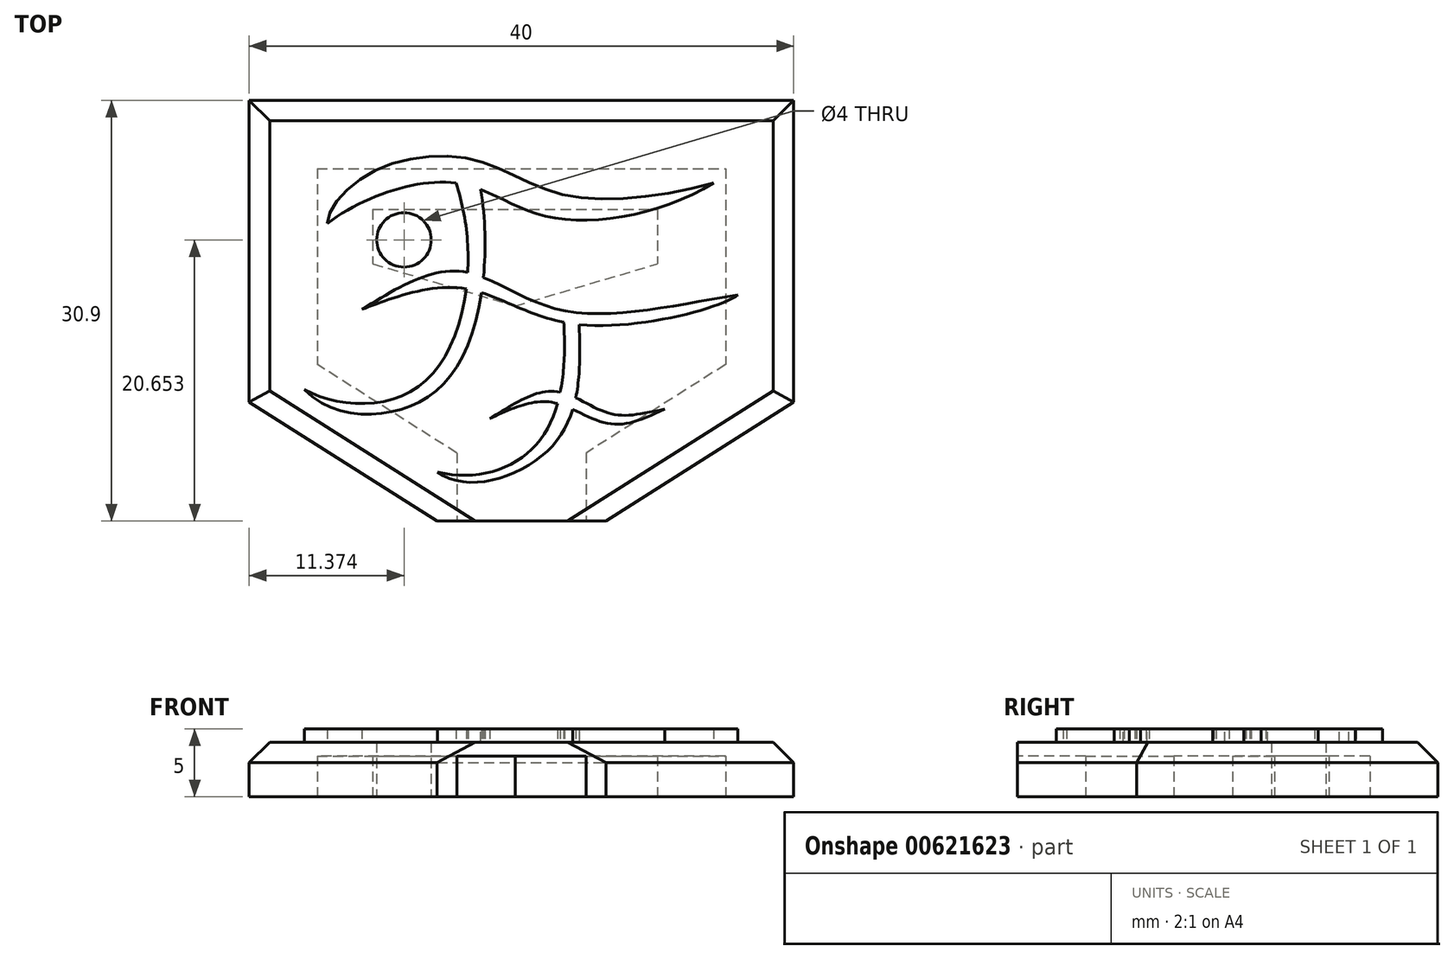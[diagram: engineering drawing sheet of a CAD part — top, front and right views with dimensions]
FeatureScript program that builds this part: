
annotation { "Feature Type Name" : "Feature", "Feature Type Description" : "" }
export const myFeature = defineFeature(function(context is Context, id is Id, definition is map)
    precondition{}
    {
        {
            var Q0;
            Q0=qCreatedBy(makeId("Top.planeOp"),FACE);
            var sketch = newSketch(context, id + "F0", { "sketchPlane" : qUnion([Q0])});
            skLineSegment(sketch, "E0.bottom", {"start": v(-43.19, 20.9) * mm, "end": v(-13.19, 20.9) * mm});
            skLineSegment(sketch, "E0.top", {"start": v(-43.19, 6.5) * mm, "end": v(-13.19, 6.5) * mm});
            skLineSegment(sketch, "E0.left", {"start": v(-43.19, 20.9) * mm, "end": v(-43.19, 6.5) * mm});
            skLineSegment(sketch, "E0.right", {"start": v(-13.19, 20.9) * mm, "end": v(-13.19, 6.5) * mm});
            skLineSegment(sketch, "E1", {"start": v(-23.44, 0) * mm, "end": v(-32.94, 0) * mm});
            skLineSegment(sketch, "E2", {"start": v(-32.94, 0) * mm, "end": v(-43.19, 6.5) * mm});
            skLineSegment(sketch, "E3", {"start": v(-13.19, 6.5) * mm, "end": v(-23.44, 0) * mm});
            skLineSegment(sketch, "E4.bottom", {"start": v(-39.1, 17.9) * mm, "end": v(-18.19, 17.9) * mm});
            skLineSegment(sketch, "E4.top", {"start": v(-39.1, 13.9) * mm, "end": v(-18.19, 13.9) * mm});
            skLineSegment(sketch, "E4.left", {"start": v(-39.1, 17.9) * mm, "end": v(-39.1, 13.9) * mm});
            skLineSegment(sketch, "E4.right", {"start": v(-18.19, 17.9) * mm, "end": v(-18.19, 13.9) * mm});
            skLineSegment(sketch, "E5", {"start": v(-39.1, 13.9) * mm, "end": v(-28.65, 10.8) * mm});
            skLineSegment(sketch, "E6", {"start": v(-28.65, 10.8) * mm, "end": v(-18.19, 13.9) * mm});
            skLineSegment(sketch, "E7.0", {"start": v(-48.19, 25.9) * mm, "end": v(-48.19, 3.75) * mm});
            skLineSegment(sketch, "E7.1", {"start": v(-8.19, 25.9) * mm, "end": v(-8.19, 3.75) * mm});
            skLineSegment(sketch, "E7.2", {"start": v(-8.19, 3.75) * mm, "end": v(-21.99, -5) * mm});
            skLineSegment(sketch, "E7.3", {"start": v(-48.19, 25.9) * mm, "end": v(-8.19, 25.9) * mm});
            skLineSegment(sketch, "E7.4", {"start": v(-21.99, -5) * mm, "end": v(-34.39, -5) * mm});
            skLineSegment(sketch, "E7.5", {"start": v(-34.39, -5) * mm, "end": v(-48.19, 3.75) * mm});
            skLineSegment(sketch, "E8", {"start": v(-23.44, 0) * mm, "end": v(-23.44, -5) * mm});
            skLineSegment(sketch, "E9", {"start": v(-32.94, 0) * mm, "end": v(-32.94, -5) * mm});
            skCircle(sketch, "E10", {"center": v(-36.82, 15.65) * mm, "radius": 2 * mm});
            skSolve(sketch);
        }
        {
            var Q0;
            Q0=makeQuery(id+"F0.imprint","IMPRINT",FACE,{"disambiguationData":[TD([[makeQuery(id+"F0.imprint","IMPRINT",EDGE,{"derivedFrom":sQuery(id+"F0.wireOp",EDGE,"E0.bottom")}),1.0]])]});
            var Q1;
            Q1=makeQuery(id+"F0.imprint","IMPRINT",FACE,{"disambiguationData":[TD([[makeQuery(id+"F0.imprint","IMPRINT",EDGE,{"derivedFrom":sQuery(id+"F0.wireOp",EDGE,"E0.bottom")}),-1.0]])]});
            var Q2;
            Q2=makeQuery(id+"F0.imprint","IMPRINT",FACE,{"disambiguationData":[TD([[makeQuery(id+"F0.imprint","IMPRINT",EDGE,{"derivedFrom":sQuery(id+"F0.wireOp",EDGE,"E0.top")}),-1.0]])]});
            var Q3;
            Q3=makeQuery(id+"F0.imprint","IMPRINT",FACE,{"disambiguationData":[TD([[makeQuery(id+"F0.imprint","IMPRINT",EDGE,{"derivedFrom":sQuery(id+"F0.wireOp",EDGE,"E1")}),1.0]])]});
            var Q4;
            Q4=makeQuery(id+"F0.imprint","IMPRINT",FACE,{"disambiguationData":[TD([[makeQuery(id+"F0.imprint","IMPRINT",EDGE,{"derivedFrom":sQuery(id+"F0.wireOp",EDGE,"E4.bottom")}),-1.0]])]});
            var Q5;
            Q5=makeQuery(id+"F0.imprint","IMPRINT",FACE,{"disambiguationData":[TD([[makeQuery(id+"F0.imprint","IMPRINT",EDGE,{"derivedFrom":sQuery(id+"F0.wireOp",EDGE,"E4.top")}),-1.0]])]});
            extrude(context, id + "F1", {"entities" : qUnion([Q0, Q1, Q2, Q3, Q4, Q5]), "depth" : 4 * mm, "offsetDistance" : 25 * mm});
        }
        {
            var Q0;
            Q0=makeQuery(id+"F0.imprint","IMPRINT",FACE,{"disambiguationData":[TD([[makeQuery(id+"F0.imprint","IMPRINT",EDGE,{"derivedFrom":sQuery(id+"F0.wireOp",EDGE,"E0.bottom")}),-1.0]])]});
            var Q1;
            Q1=makeQuery(id+"F0.imprint","IMPRINT",FACE,{"disambiguationData":[TD([[makeQuery(id+"F0.imprint","IMPRINT",EDGE,{"derivedFrom":sQuery(id+"F0.wireOp",EDGE,"E0.top")}),-1.0]])]});
            var Q2;
            Q2=makeQuery(id+"F0.imprint","IMPRINT",FACE,{"disambiguationData":[TD([[makeQuery(id+"F0.imprint","IMPRINT",EDGE,{"derivedFrom":sQuery(id+"F0.wireOp",EDGE,"E1")}),1.0]])]});
            extrude(context, id + "F2", {"entities" : qUnion([Q0, Q1, Q2]), "operationType" : NewBodyOperationType.REMOVE, "depth" : 3 * mm, "offsetDistance" : 25 * mm});
        }
        {
            var Q0;
            Q0=makeQuery(id+"F1.opExtrude","CAP_FACE",FACE,{"disambiguationData":[OSD([sQuery(id+"F0.wireOp",EDGE,"E4.bottom"),sQuery(id+"F0.wireOp",EDGE,"E4.left"),sQuery(id+"F0.wireOp",EDGE,"E4.right"),sQuery(id+"F0.wireOp",EDGE,"E5"),sQuery(id+"F0.wireOp",EDGE,"E6"),sQuery(id+"F0.wireOp",EDGE,"E7.0"),sQuery(id+"F0.wireOp",EDGE,"E7.1"),sQuery(id+"F0.wireOp",EDGE,"E7.2"),sQuery(id+"F0.wireOp",EDGE,"E7.3"),sQuery(id+"F0.wireOp",EDGE,"E7.4"),sQuery(id+"F0.wireOp",EDGE,"E7.5")])],"isStart":false});
            var sketch = newSketch(context, id + "F3", { "sketchPlane" : qUnion([Q0])});
            skLineSegment(sketch, "E11.bottom", {"start": v(-48.19, 25.9) * mm, "end": v(-8.19, 25.9) * mm});
            skLineSegment(sketch, "E11.top", {"start": v(-48.19, 25.9) * mm, "end": v(-8.19, 25.9) * mm});
            skLineSegment(sketch, "E11.left", {"start": v(-48.19, 25.9) * mm, "end": v(-48.19, 25.9) * mm});
            skLineSegment(sketch, "E11.right", {"start": v(-8.19, 25.9) * mm, "end": v(-8.19, 25.9) * mm});
            skLineSegment(sketch, "E12", {"start": v(-8.19, 25.9) * mm, "end": v(-8.19, 3.75) * mm});
            skLineSegment(sketch, "E13", {"start": v(-8.19, 3.75) * mm, "end": v(-21.99, -5) * mm});
            skLineSegment(sketch, "E14", {"start": v(-21.99, -5) * mm, "end": v(-34.39, -5) * mm});
            skLineSegment(sketch, "E15", {"start": v(-34.39, -5) * mm, "end": v(-48.19, 3.75) * mm});
            skLineSegment(sketch, "E16", {"start": v(-48.19, 3.75) * mm, "end": v(-48.19, 25.9) * mm});
            skFitSpline(sketch, "E17", {"points": [v(-33, 19.84) * mm, v(-35.47, 5.1) * mm, v(-44.14, 4.67) * mm], "startDerivative": vector(9.5, -28.07) * mm, "endDerivative": vector(-16.18, 9.06) * mm});
            skFitSpline(sketch, "E18", {"points": [v(-42.47, 16.85) * mm, v(-33, 19.84) * mm, v(-26.28, 17.36) * mm, v(-14.05, 19.84) * mm], "startDerivative": vector(23.8, 17.85) * mm, "endDerivative": vector(29.47, 18.05) * mm});
            skFitSpline(sketch, "E19", {"points": [v(-42.47, 16.85) * mm, v(-39.43, 20.49) * mm, v(-31.78, 21.56) * mm, v(-25.2, 19) * mm, v(-14.05, 19.84) * mm], "startDerivative": vector(1.4, 17.51) * mm, "endDerivative": vector(37.91, 10.12) * mm});
            skFitSpline(sketch, "E20", {"points": [v(-44.14, 4.67) * mm, v(-37.9, 3) * mm, v(-32.71, 6.68) * mm, v(-31.17, 19.35) * mm], "startDerivative": vector(17.4, -17.89) * mm, "endDerivative": vector(-5.22, 32.67) * mm});
            skFitSpline(sketch, "E21", {"points": [v(-39.9, 10.55) * mm, v(-32.8, 12.14) * mm, v(-23.94, 9.43) * mm, v(-12.28, 11.62) * mm], "startDerivative": vector(17.37, 6.5) * mm, "endDerivative": vector(9.06, 7.67) * mm});
            skFitSpline(sketch, "E22", {"points": [v(-39.9, 10.55) * mm, v(-32.76, 13.35) * mm, v(-25.48, 10.55) * mm, v(-12.28, 11.62) * mm], "startDerivative": vector(24.19, 14.86) * mm, "endDerivative": vector(35.03, 5.66) * mm});
            skFitSpline(sketch, "E23", {"points": [v(-25.08, 9.6) * mm, v(-26.8, 0.99) * mm, v(-34.35, -1.4) * mm], "startDerivative": vector(1.09, -16.14) * mm, "endDerivative": vector(-18.1, 4.6) * mm});
            skFitSpline(sketch, "E24", {"points": [v(-23.94, 9.43) * mm, v(-26.04, 0.38) * mm, v(-34.35, -1.4) * mm], "startDerivative": vector(0.82, -20.8) * mm, "endDerivative": vector(-13.56, 10.24) * mm});
            skFitSpline(sketch, "E25", {"points": [v(-30.52, 2.53) * mm, v(-26.04, 3.74) * mm, v(-21.98, 2.2) * mm, v(-17.65, 3.23) * mm], "startDerivative": vector(13.93, 6.35) * mm, "endDerivative": vector(15.57, 7.58) * mm});
            skFitSpline(sketch, "E26", {"points": [v(-30.52, 2.53) * mm, v(-25.86, 4.53) * mm, v(-21.98, 3) * mm, v(-17.65, 3.23) * mm], "startDerivative": vector(13.93, 8.23) * mm, "endDerivative": vector(18.42, 3.85) * mm});
            skSolve(sketch);
        }
        {
            var Q0;
            {var subQ0=sQuery(id+"F3.wireOp",EDGE,"E19");Q0=makeQuery(id+"F3.imprint","IMPRINT",FACE,{"disambiguationData":[TD([[makeQuery(id+"F3.imprint","IMPRINT",EDGE,{"derivedFrom":subQ0}),-1.0]])]});}
            var Q1;
            {var subQ0=sQuery(id+"F3.wireOp",EDGE,"E18");var subQ1=makeQuery(id+"F1.opExtrude","CAP_EDGE",EDGE,{"disambiguationData":[OSD([sQuery(id+"F0.wireOp",EDGE,"E4.bottom")])],"isStart":false});var subQ2=makeQuery(id+"F3.imprint","INTERSECT",VERTEX,{"disambiguationData":[OD(0.0)],"derivedFrom":[subQ1,subQ0]});Q1=makeQuery(id+"F3.imprint","IMPRINT",FACE,{"disambiguationData":[TD([[makeQuery(id+"F3.imprint","IMPRINT",EDGE,{"disambiguationData":[TD([[subQ2,-1.0]])],"derivedFrom":subQ0}),1.0]])]});}
            var Q2;
            {var subQ0=sQuery(id+"F3.wireOp",EDGE,"E22");var subQ1=sQuery(id+"F3.wireOp",EDGE,"E17");var subQ2=makeQuery(id+"F3.imprint","INTERSECT",VERTEX,{"derivedFrom":[subQ1,subQ0]});Q2=makeQuery(id+"F3.imprint","IMPRINT",FACE,{"disambiguationData":[TD([[makeQuery(id+"F3.imprint","IMPRINT",EDGE,{"disambiguationData":[TD([[subQ2,1.0]])],"derivedFrom":subQ1}),1.0]])]});}
            var Q3;
            {var subQ0=sQuery(id+"F3.wireOp",EDGE,"E18");var subQ1=sQuery(id+"F3.wireOp",EDGE,"E17");var subQ2=makeQuery(id+"F3.imprint","INTERSECT",VERTEX,{"derivedFrom":[subQ1,subQ0]});Q3=makeQuery(id+"F3.imprint","IMPRINT",FACE,{"disambiguationData":[TD([[makeQuery(id+"F3.imprint","IMPRINT",EDGE,{"disambiguationData":[TD([[subQ2,-1.0]])],"derivedFrom":subQ1}),1.0]])]});}
            var Q4;
            {var subQ0=sQuery(id+"F3.wireOp",EDGE,"E22");var subQ1=sQuery(id+"F3.wireOp",EDGE,"E17");var subQ2=makeQuery(id+"F3.imprint","INTERSECT",VERTEX,{"derivedFrom":[subQ1,subQ0]});Q4=makeQuery(id+"F3.imprint","IMPRINT",FACE,{"disambiguationData":[TD([[makeQuery(id+"F3.imprint","IMPRINT",EDGE,{"disambiguationData":[TD([[subQ2,-1.0]])],"derivedFrom":subQ1}),-1.0]])]});}
            var Q5;
            {var subQ0=sQuery(id+"F3.wireOp",EDGE,"E22");var subQ1=sQuery(id+"F3.wireOp",EDGE,"E21");var subQ2=makeQuery(id+"F3.imprint","INTERSECT",VERTEX,{"disambiguationData":[OD(0.0)],"derivedFrom":[subQ1,subQ0]});Q5=makeQuery(id+"F3.imprint","IMPRINT",FACE,{"disambiguationData":[TD([[makeQuery(id+"F3.imprint","IMPRINT",EDGE,{"disambiguationData":[TD([[subQ2,-1.0]])],"derivedFrom":subQ1}),1.0]])]});}
            var Q6;
            {var subQ0=sQuery(id+"F3.wireOp",EDGE,"E21");var subQ1=sQuery(id+"F3.wireOp",EDGE,"E20");var subQ2=makeQuery(id+"F3.imprint","INTERSECT",VERTEX,{"derivedFrom":[subQ1,subQ0]});Q6=makeQuery(id+"F3.imprint","IMPRINT",FACE,{"disambiguationData":[TD([[makeQuery(id+"F3.imprint","IMPRINT",EDGE,{"disambiguationData":[TD([[subQ2,-1.0]])],"derivedFrom":subQ1}),-1.0]])]});}
            var Q7;
            {var subQ0=sQuery(id+"F3.wireOp",EDGE,"E22");var subQ1=sQuery(id+"F3.wireOp",EDGE,"E17");var subQ2=makeQuery(id+"F3.imprint","INTERSECT",VERTEX,{"derivedFrom":[subQ1,subQ0]});Q7=makeQuery(id+"F3.imprint","IMPRINT",FACE,{"disambiguationData":[TD([[makeQuery(id+"F3.imprint","IMPRINT",EDGE,{"disambiguationData":[TD([[subQ2,-1.0]])],"derivedFrom":subQ1}),1.0]])]});}
            var Q8;
            {var subQ0=sQuery(id+"F3.wireOp",EDGE,"E20");var subQ1=sQuery(id+"F3.wireOp",EDGE,"E17");var subQ2=makeQuery(id+"F3.imprint","INTERSECT",VERTEX,{"derivedFrom":[subQ1,subQ0]});Q8=makeQuery(id+"F3.imprint","IMPRINT",FACE,{"disambiguationData":[TD([[makeQuery(id+"F3.imprint","IMPRINT",EDGE,{"disambiguationData":[TD([[subQ2,1.0]])],"derivedFrom":subQ1}),1.0]])]});}
            var Q9;
            {var subQ0=sQuery(id+"F3.wireOp",EDGE,"E21");var subQ1=sQuery(id+"F3.wireOp",EDGE,"E17");var subQ2=makeQuery(id+"F3.imprint","INTERSECT",VERTEX,{"derivedFrom":[subQ1,subQ0]});Q9=makeQuery(id+"F3.imprint","IMPRINT",FACE,{"disambiguationData":[TD([[makeQuery(id+"F3.imprint","IMPRINT",EDGE,{"disambiguationData":[TD([[subQ2,-1.0]])],"derivedFrom":subQ1}),1.0]])]});}
            var Q10;
            {var subQ1=sQuery(id+"F3.wireOp",EDGE,"E21");var subQ6=makeQuery(id+"F3.imprint","INTERSECT",VERTEX,{"derivedFrom":[subQ1,sQuery(id+"F3.wireOp",EDGE,"E23")]});Q10=makeQuery(id+"F3.imprint","IMPRINT",FACE,{"disambiguationData":[TD([[makeQuery(id+"F3.imprint","IMPRINT",EDGE,{"disambiguationData":[TD([[subQ6,1.0]])],"derivedFrom":subQ1}),1.0]])]});}
            var Q11;
            {var subQ0=sQuery(id+"F3.wireOp",EDGE,"E23");var subQ1=sQuery(id+"F3.wireOp",EDGE,"E21");var subQ2=makeQuery(id+"F3.imprint","INTERSECT",VERTEX,{"derivedFrom":[subQ1,subQ0]});Q11=makeQuery(id+"F3.imprint","IMPRINT",FACE,{"disambiguationData":[TD([[makeQuery(id+"F3.imprint","IMPRINT",EDGE,{"disambiguationData":[TD([[subQ2,-1.0]])],"derivedFrom":subQ1}),-1.0]])]});}
            var Q12;
            {var subQ0=sQuery(id+"F3.wireOp",EDGE,"E26");var subQ1=sQuery(id+"F3.wireOp",EDGE,"E24");var subQ2=makeQuery(id+"F3.imprint","INTERSECT",VERTEX,{"derivedFrom":[subQ1,subQ0]});Q12=makeQuery(id+"F3.imprint","IMPRINT",FACE,{"disambiguationData":[TD([[makeQuery(id+"F3.imprint","IMPRINT",EDGE,{"disambiguationData":[TD([[subQ2,-1.0]])],"derivedFrom":subQ1}),1.0]])]});}
            var Q13;
            {var subQ0=sQuery(id+"F3.wireOp",EDGE,"E26");var subQ1=sQuery(id+"F3.wireOp",EDGE,"E23");var subQ2=makeQuery(id+"F3.imprint","INTERSECT",VERTEX,{"derivedFrom":[subQ1,subQ0]});Q13=makeQuery(id+"F3.imprint","IMPRINT",FACE,{"disambiguationData":[TD([[makeQuery(id+"F3.imprint","IMPRINT",EDGE,{"disambiguationData":[TD([[subQ2,-1.0]])],"derivedFrom":subQ1}),1.0]])]});}
            var Q14;
            {var subQ0=sQuery(id+"F3.wireOp",EDGE,"E26");var subQ1=sQuery(id+"F3.wireOp",EDGE,"E23");var subQ2=makeQuery(id+"F3.imprint","INTERSECT",VERTEX,{"derivedFrom":[subQ1,subQ0]});Q14=makeQuery(id+"F3.imprint","IMPRINT",FACE,{"disambiguationData":[TD([[makeQuery(id+"F3.imprint","IMPRINT",EDGE,{"disambiguationData":[TD([[subQ2,-1.0]])],"derivedFrom":subQ1}),-1.0]])]});}
            var Q15;
            {var subQ0=sQuery(id+"F3.wireOp",EDGE,"E24");var subQ1=sQuery(id+"F3.wireOp",EDGE,"E23");var subQ2=makeQuery(id+"F3.imprint","INTERSECT",VERTEX,{"derivedFrom":[subQ1,subQ0]});Q15=makeQuery(id+"F3.imprint","IMPRINT",FACE,{"disambiguationData":[TD([[makeQuery(id+"F3.imprint","IMPRINT",EDGE,{"disambiguationData":[TD([[subQ2,1.0]])],"derivedFrom":subQ1}),1.0]])]});}
            extrude(context, id + "F4", {"entities" : qUnion([Q0, Q1, Q2, Q3, Q4, Q5, Q6, Q7, Q8, Q9, Q10, Q11, Q12, Q13, Q14, Q15]), "depth" : 1 * mm, "offsetDistance" : 25 * mm});
        }
        {
            var Q0;
            Q0=makeQuery(id+"F1.opExtrude","CAP_EDGE",EDGE,{"disambiguationData":[OSD([sQuery(id+"F0.wireOp",EDGE,"E7.5")])],"isStart":false});
            var Q1;
            Q1=makeQuery(id+"F1.opExtrude","CAP_EDGE",EDGE,{"disambiguationData":[OSD([sQuery(id+"F0.wireOp",EDGE,"E7.0")])],"isStart":false});
            var Q2;
            Q2=makeQuery(id+"F1.opExtrude","CAP_EDGE",EDGE,{"disambiguationData":[OSD([sQuery(id+"F0.wireOp",EDGE,"E7.3")])],"isStart":false});
            var Q3;
            Q3=makeQuery(id+"F1.opExtrude","CAP_EDGE",EDGE,{"disambiguationData":[OSD([sQuery(id+"F0.wireOp",EDGE,"E7.1")])],"isStart":false});
            var Q4;
            Q4=makeQuery(id+"F1.opExtrude","CAP_EDGE",EDGE,{"disambiguationData":[OSD([sQuery(id+"F0.wireOp",EDGE,"E7.2")])],"isStart":false});
            chamfer(context, id + "F5", {"entities" : qUnion([Q0, Q1, Q2, Q3, Q4]), "width" : 1.5 * mm, "tangentPropagation" : true});
        }
    });
